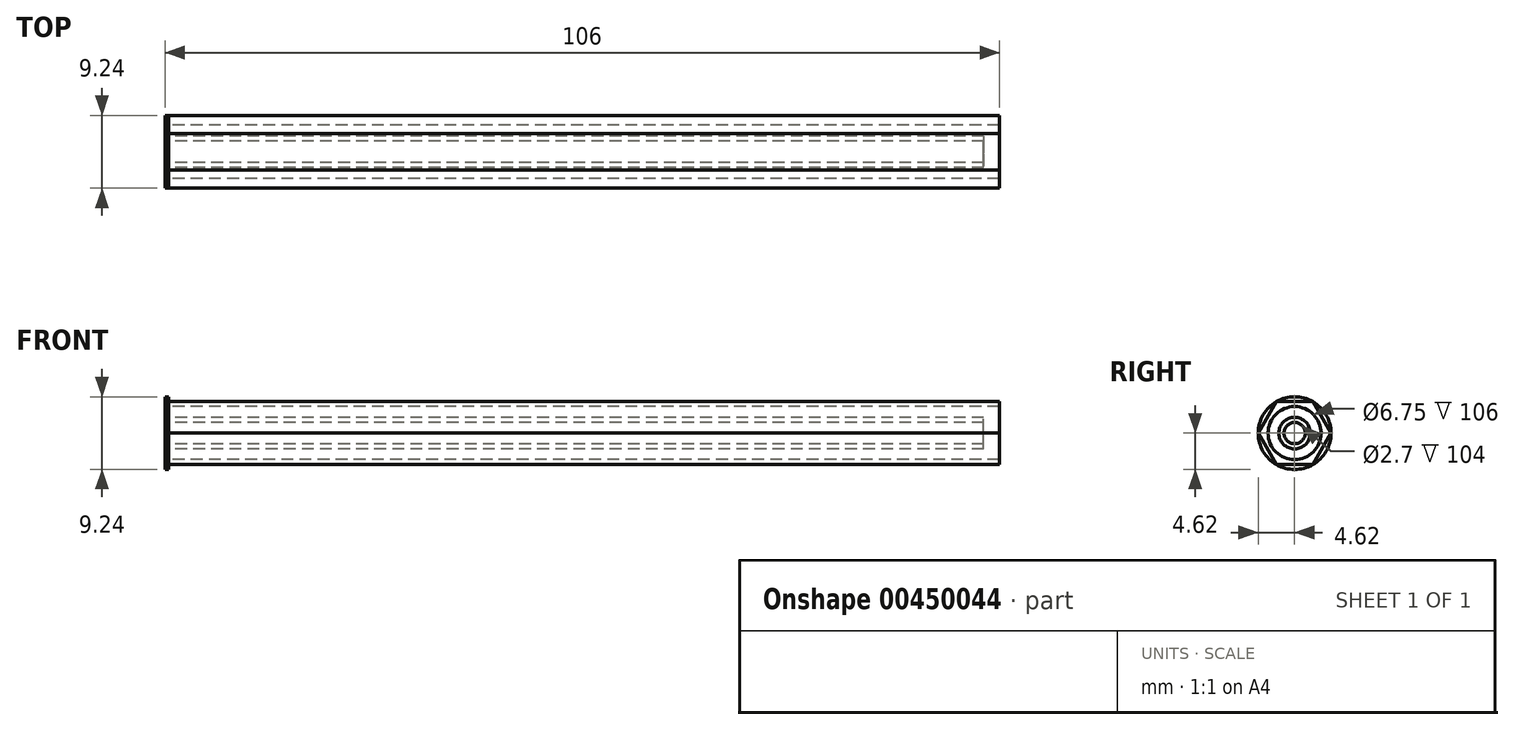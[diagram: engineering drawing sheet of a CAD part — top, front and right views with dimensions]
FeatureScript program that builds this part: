
annotation { "Feature Type Name" : "Feature", "Feature Type Description" : "" }
export const myFeature = defineFeature(function(context is Context, id is Id, definition is map)
    precondition{}
    {
        {
            var Q0;
            Q0=qCreatedBy(makeId("Right.planeOp"),FACE);
            var sketch = newSketch(context, id + "F0", { "sketchPlane" : qUnion([Q0])});
            skCircle(sketch, "E0", {"center": v(0, 0) * mm, "radius": 2 * mm});
            skCircle(sketch, "E1", {"center": v(0, 0) * mm, "radius": 1.35 * mm});
            skSolve(sketch);
        }
        {
            var Q0;
            Q0=makeQuery(id+"F0.imprint","IMPRINT",FACE,{"disambiguationData":[TD([[makeQuery(id+"F0.imprint","IMPRINT",EDGE,{"derivedFrom":sQuery(id+"F0.wireOp",EDGE,"E0")}),1.0]])]});
            extrude(context, id + "F1", {"entities" : qUnion([Q0]), "depth" : 104 * mm});
        }
        {
            var Q0;
            Q0=qCreatedBy(makeId("Right.planeOp"),FACE);
            var sketch = newSketch(context, id + "F2", { "sketchPlane" : qUnion([Q0])});
            skCircle(sketch, "E2.cCircle", {"center": v(0, 0) * mm, "radius": 4 * mm, "construction": true});
            skLineSegment(sketch, "E2.0", {"start": v(-4.62, 0) * mm, "end": v(-2.3, 4) * mm});
            skLineSegment(sketch, "E2.1", {"start": v(-2.3, 4) * mm, "end": v(2.3, 4) * mm});
            skLineSegment(sketch, "E2.2", {"start": v(2.3, 4) * mm, "end": v(4.62, 0) * mm});
            skLineSegment(sketch, "E2.3", {"start": v(4.62, 0) * mm, "end": v(2.3, -4) * mm});
            skLineSegment(sketch, "E2.4", {"start": v(2.3, -4) * mm, "end": v(-2.3, -4) * mm});
            skLineSegment(sketch, "E2.5", {"start": v(-2.3, -4) * mm, "end": v(-4.62, 0) * mm});
            skPoint(sketch, "E2.0.midPoint", {"position": v(-3.46, 2) * mm});
            skCircle(sketch, "E3", {"center": v(0, 0) * mm, "radius": 3.38 * mm});
            skSolve(sketch);
        }
        {
            var Q0;
            Q0=makeQuery(id+"F2.imprint","IMPRINT",FACE,{"disambiguationData":[TD([[makeQuery(id+"F2.imprint","IMPRINT",EDGE,{"derivedFrom":sQuery(id+"F2.wireOp",EDGE,"E2.0")}),-1.0]])]});
            extrude(context, id + "F3", {"entities" : qUnion([Q0]), "depth" : 106 * mm});
        }
        {
            var Q0;
            Q0=qCreatedBy(makeId("Right.planeOp"),FACE);
            var sketch = newSketch(context, id + "F4", { "sketchPlane" : qUnion([Q0])});
            skCircle(sketch, "E4", {"center": v(0, 0) * mm, "radius": 4.62 * mm});
            skCircle(sketch, "E5", {"center": v(0, 0) * mm, "radius": 3.38 * mm});
            skSolve(sketch);
        }
        {
            var Q0;
            Q0=makeQuery(id+"F4.imprint","IMPRINT",FACE,{"disambiguationData":[TD([[makeQuery(id+"F4.imprint","IMPRINT",EDGE,{"derivedFrom":sQuery(id+"F4.wireOp",EDGE,"E4")}),1.0]])]});
            extrude(context, id + "F5", {"entities" : qUnion([Q0]), "operationType" : NewBodyOperationType.ADD, "depth" : 0.5 * mm});
        }
    });
